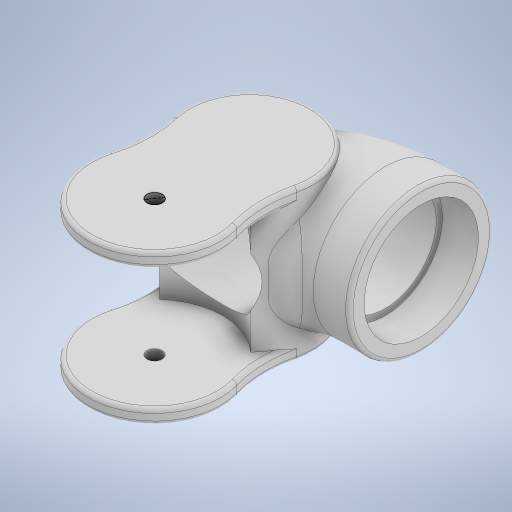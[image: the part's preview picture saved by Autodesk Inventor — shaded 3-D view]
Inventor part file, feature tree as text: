
AUTODESK INVENTOR PART (.ipt)
format: ipt  version: 2024 (Build 280153000, 153)  size: 550,912 bytes
history: native  units: mm
features: extrude x9, fillet x6, plane x4, sketch x3, revolve x2, projected_geometry x2
ambient origin geometry x8: Origin, YZ Plane, XZ Plane, XY Plane, X Axis, Y Axis, Z Axis, Center Point
bodies: Solid1 (feature_tree)
feature tree (26):
  plane  "Work Plane1"
  plane  "Work Plane2"
  extrude  "Extrusion1"  Depth=70.0mm
  extrude  "Extrusion2"  Depth=70.0mm
  extrude  "Extrusion8"  Depth=2.0mm
  extrude  "Extrusion9"  TaperAngle=0.0deg  [1 undecoded]
  plane  "Work Plane4"
  extrude  "Extrusion10"  Depth=10.0mm TaperAngle=0.0deg
  plane  "Work Plane5"
  sketch  "Sketch17"  dims[d3=7.5mm d4=0.0mm d5=70.0mm]
  revolve  "Revolution4"  [1 undecoded]
  extrude  "Extrusion11"  Depth=2.0mm
  revolve  "Revolution5"  [1 undecoded]
  extrude  "Extrusion13"  Depth=52.0mm
  extrude  "Extrusion14"  Depth=2.0mm
  extrude  "Extrusion15"  Depth=10.0mm TaperAngle=0.0deg
  fillet  "Fillet9"  Radius=44.75mm
  fillet  "Fillet10"  Radius=54.0mm
  fillet  "Fillet11"  Radius=77.0mm
  fillet  "Fillet12"  [1 undecoded]
  fillet  "Fillet13"  Radius=76.0mm
  fillet  "Fillet14"  Radius=72.0mm
  sketch  "Sketch13"  dims[d0=32.0mm d1=-32.0mm d2=70.0mm]
  sketch  "Sketch22"  dims[d6=7.5mm d7=0.0mm d36=8.0mm d37=0.0mm d38=0.0mm d43=10.0mm d44=0.0mm d48=26.0mm d49=26.0mm d52=-37.5mm d53=52.0mm d54=130.0mm d55=10.0mm d56=0.0mm d57=44.75mm d59=54.0mm d61=77.0mm d62=90.0deg d63=76.0mm d64=72.0mm d65=0.0mm d66=0.0mm d67=45.0mm d73=19.198622mm d74=60.325mm d75=76.0mm d76=19.05mm d77=0.0mm d78=7.5mm d79=0.0mm d80=7.5mm d81=0.0mm d87=28.0mm d88=17.5mm d89=63.0mm d90=63.0mm d91=2.0mm d92=2.0mm d32=0.0mm d33=0.0mm d34=0.0mm d35=0.0mm]
  projected_geometry  "Projected Loop3"
  projected_geometry  "Projected Loop4"
note: 4 required parameter values undecoded (feature->parameter linkage not recoverable at this tier; creation-order binding heuristic only, values carry confidence <= 0.55)